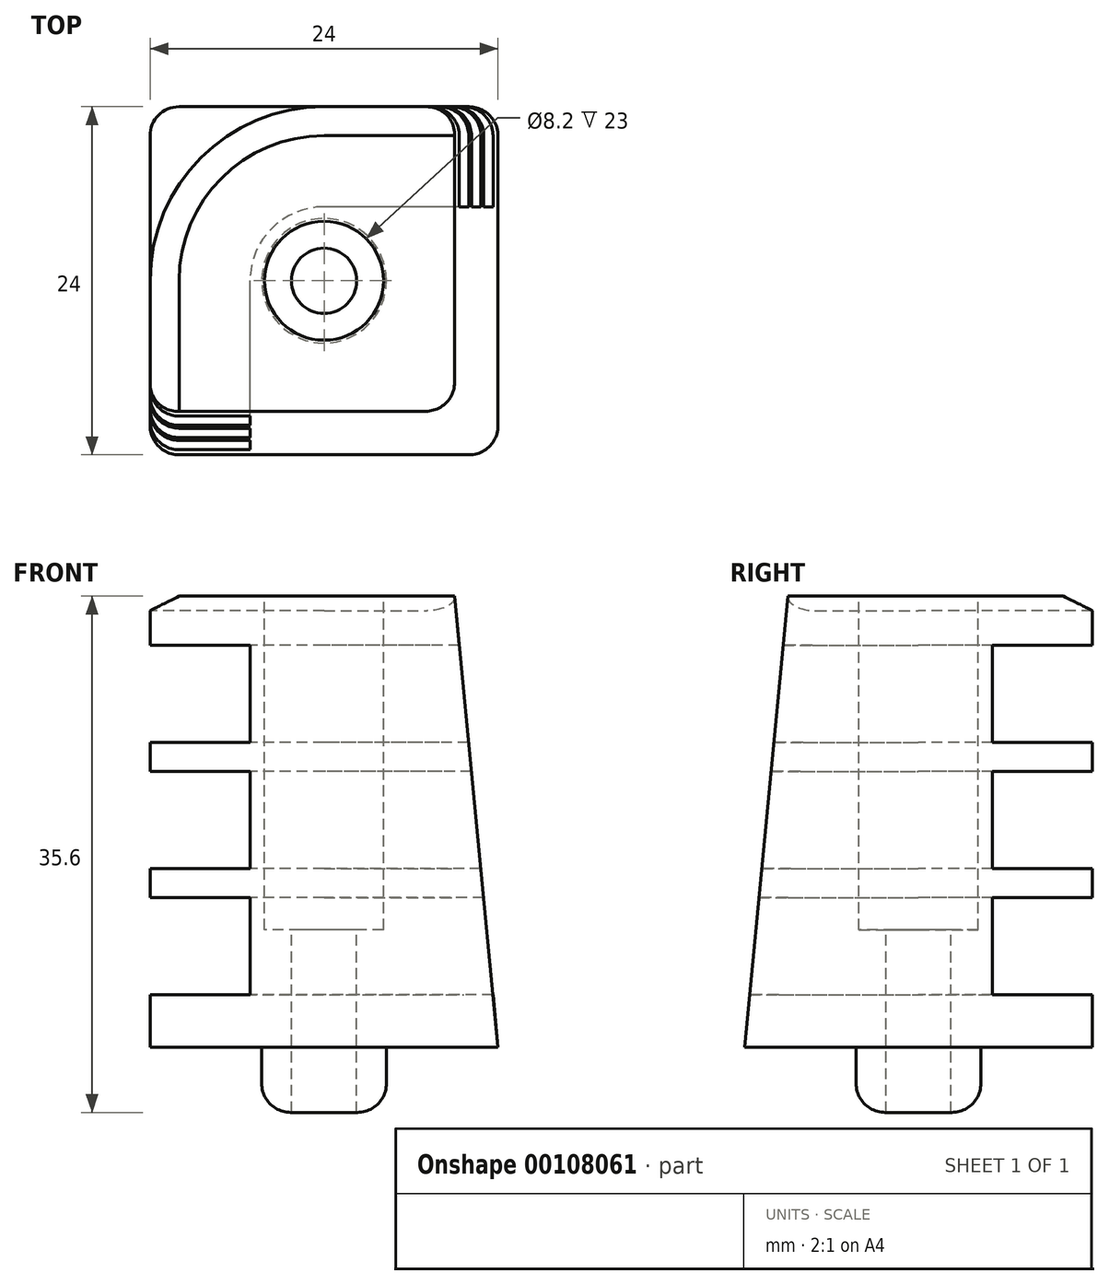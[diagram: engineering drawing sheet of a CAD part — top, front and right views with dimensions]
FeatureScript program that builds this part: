
annotation { "Feature Type Name" : "Feature", "Feature Type Description" : "" }
export const myFeature = defineFeature(function(context is Context, id is Id, definition is map)
    precondition{}
    {
        {
            var Q0;
            Q0=qCreatedBy(makeId("Top.planeOp"),FACE);
            var sketch = newSketch(context, id + "F0", { "sketchPlane" : qUnion([Q0])});
            skLineSegment(sketch, "E0.bottom", {"start": v(0, 0) * mm, "end": v(24, 0) * mm});
            skLineSegment(sketch, "E0.top", {"start": v(0, 24) * mm, "end": v(24, 24) * mm});
            skLineSegment(sketch, "E0.left", {"start": v(0, 0) * mm, "end": v(0, 24) * mm});
            skLineSegment(sketch, "E0.right", {"start": v(24, 0) * mm, "end": v(24, 24) * mm});
            skPoint(sketch, "E1.visualSharp", {"position": v(0, 24) * mm});
            skPoint(sketch, "E2.visualSharp", {"position": v(24, 24) * mm});
            skPoint(sketch, "E3.visualSharp", {"position": v(24, 0) * mm});
            skPoint(sketch, "E4.visualSharp", {"position": v(0, 0) * mm});
            skSolve(sketch);
        }
        {
            var Q0;
            Q0 = qSketchRegion(id + "F0", true);
            extrude(context, id + "F1", {"entities" : qUnion([Q0]), "depth" : 3.6 * mm});
        }
        {
            var Q0;
            Q0=makeQuery(id+"F1.opExtrude","CAP_FACE",FACE,{"disambiguationData":[OSD([sQuery(id+"F0.wireOp",EDGE,"E0.bottom"),sQuery(id+"F0.wireOp",EDGE,"E0.top"),sQuery(id+"F0.wireOp",EDGE,"E0.left"),sQuery(id+"F0.wireOp",EDGE,"E0.right"),sQuery(id+"F0.wireOp",EDGE,"E1.filletArc"),sQuery(id+"F0.wireOp",EDGE,"E2.filletArc"),sQuery(id+"F0.wireOp",EDGE,"E3.filletArc"),sQuery(id+"F0.wireOp",EDGE,"E4.filletArc")])],"isStart":true});
            var sketch = newSketch(context, id + "F2", { "sketchPlane" : qUnion([Q0])});
            skPoint(sketch, "E5.centerSnap0", {"position": v(12, -24) * mm});
            skPoint(sketch, "E6", {"position": v(24, -12) * mm});
            skCircle(sketch, "E7", {"center": v(12, -12) * mm, "radius": 4.3 * mm});
            skCircle(sketch, "E8", {"center": v(12, -12) * mm, "radius": 2.25 * mm});
            skSolve(sketch);
        }
        {
            var Q0;
            Q0=makeQuery(id+"F2.imprint","IMPRINT",FACE,{"disambiguationData":[TD([[makeQuery(id+"F2.imprint","IMPRINT",EDGE,{"derivedFrom":sQuery(id+"F2.wireOp",EDGE,"E7")}),1.0]])]});
            extrude(context, id + "F3", {"entities" : qUnion([Q0]), "operationType" : NewBodyOperationType.ADD, "depth" : 4.5 * mm});
        }
        {
            var Q0;
            Q0=makeQuery(id+"F3.boolean.opBoolean","SPLIT",FACE,{"disambiguationData":[TD([makeQuery(id+"F3.opExtrude","SWEPT_FACE",FACE,{"disambiguationData":[OSD([sQuery(id+"F2.wireOp",EDGE,"E8")])]})])],"derivedFrom":makeQuery(id+"F1.opExtrude","CAP_FACE",FACE,{"disambiguationData":[OSD([sQuery(id+"F0.wireOp",EDGE,"E0.bottom"),sQuery(id+"F0.wireOp",EDGE,"E0.top"),sQuery(id+"F0.wireOp",EDGE,"E0.left"),sQuery(id+"F0.wireOp",EDGE,"E0.right"),sQuery(id+"F0.wireOp",EDGE,"E1.filletArc"),sQuery(id+"F0.wireOp",EDGE,"E2.filletArc"),sQuery(id+"F0.wireOp",EDGE,"E3.filletArc")])],"isStart":true})});
            extrude(context, id + "F4", {"entities" : qUnion([Q0]), "operationType" : NewBodyOperationType.REMOVE, "oppositeDirection" : true, "depth" : 10 * mm});
        }
        {
            var Q0;
            Q0=makeQuery(id+"F1.opExtrude","CAP_FACE",FACE,{"disambiguationData":[OSD([sQuery(id+"F0.wireOp",EDGE,"E0.bottom"),sQuery(id+"F0.wireOp",EDGE,"E0.top"),sQuery(id+"F0.wireOp",EDGE,"E0.left"),sQuery(id+"F0.wireOp",EDGE,"E0.right"),sQuery(id+"F0.wireOp",EDGE,"E1.filletArc"),sQuery(id+"F0.wireOp",EDGE,"E2.filletArc"),sQuery(id+"F0.wireOp",EDGE,"E3.filletArc"),sQuery(id+"F0.wireOp",EDGE,"E4.filletArc")])],"isStart":false});
            var sketch = newSketch(context, id + "F5", { "sketchPlane" : qUnion([Q0])});
            skLineSegment(sketch, "E9.bottom", {"start": v(20, 0) * mm, "end": v(6.9, 0) * mm});
            skLineSegment(sketch, "E9.top", {"start": v(24, 17.1) * mm, "end": v(6.9, 17.1) * mm});
            skLineSegment(sketch, "E9.right", {"start": v(6.9, 0) * mm, "end": v(6.9, 17.1) * mm});
            skPoint(sketch, "E10.orphan", {"position": v(24, 0) * mm});
            skPoint(sketch, "E11.center.orphan", {"position": v(12, 12) * mm});
            skSolve(sketch);
        }
        {
            var Q0;
            {var subQ6=sQuery(id+"F5.wireOp",EDGE,"E9.bottom");Q0=makeQuery(id+"F5.imprint","IMPRINT",FACE,{"disambiguationData":[TD([[makeQuery(id+"F5.imprint","IMPRINT",EDGE,{"derivedFrom":subQ6}),1.0]])]});}
            extrude(context, id + "F6", {"entities" : qUnion([Q0]), "operationType" : NewBodyOperationType.ADD, "depth" : 6.7 * mm});
        }
        {
            var Q0;
            Q0=makeQuery(id+"F6.opExtrude","CAP_FACE",FACE,{"disambiguationData":[OSD([sQuery(id+"F0.wireOp",EDGE,"E0.bottom"),sQuery(id+"F0.wireOp",EDGE,"E0.top"),sQuery(id+"F0.wireOp",EDGE,"E0.left"),sQuery(id+"F0.wireOp",EDGE,"E0.right"),sQuery(id+"F2.wireOp",EDGE,"E8"),sQuery(id+"F5.wireOp",EDGE,"E9.bottom"),sQuery(id+"F5.wireOp",EDGE,"E9.top"),sQuery(id+"F5.wireOp",EDGE,"E9.right")])],"isStart":false});
            var sketch = newSketch(context, id + "F7", { "sketchPlane" : qUnion([Q0])});
            skLineSegment(sketch, "E12.bottom", {"start": v(0, 0) * mm, "end": v(24, 0) * mm});
            skLineSegment(sketch, "E12.top", {"start": v(0, 24) * mm, "end": v(24, 24) * mm});
            skLineSegment(sketch, "E12.left", {"start": v(0, 0) * mm, "end": v(0, 24) * mm});
            skLineSegment(sketch, "E12.right", {"start": v(24, 0) * mm, "end": v(24, 24) * mm});
            skSolve(sketch);
        }
        {
            var Q0;
            {var subQ2=sQuery(id+"F7.wireOp",EDGE,"E12.top");Q0=makeQuery(id+"F7.imprint","IMPRINT",FACE,{"disambiguationData":[TD([[makeQuery(id+"F7.imprint","IMPRINT",EDGE,{"derivedFrom":subQ2}),-1.0]])]});}
            var Q1;
            {var subQ1=makeQuery(id+"F6.opExtrude","CAP_EDGE",EDGE,{"disambiguationData":[OSD([sQuery(id+"F5.wireOp",EDGE,"E9.top")])],"isStart":false});Q1=makeQuery(id+"F7.imprint","IMPRINT",FACE,{"disambiguationData":[TD([[makeQuery(id+"F7.imprint","IMPRINT",EDGE,{"derivedFrom":subQ1}),1.0]])]});}
            extrude(context, id + "F8", {"entities" : qUnion([Q0, Q1]), "operationType" : NewBodyOperationType.ADD, "depth" : 2 * mm});
        }
        {
            var Q0;
            Q0=makeQuery(id+"F8.opExtrude","CAP_FACE",FACE,{"disambiguationData":[OSD([sQuery(id+"F0.wireOp",EDGE,"E0.bottom"),sQuery(id+"F0.wireOp",EDGE,"E0.top"),sQuery(id+"F0.wireOp",EDGE,"E0.left"),sQuery(id+"F0.wireOp",EDGE,"E0.right"),sQuery(id+"F2.wireOp",EDGE,"E8"),sQuery(id+"F7.wireOp",EDGE,"E12.bottom"),sQuery(id+"F7.wireOp",EDGE,"E12.top"),sQuery(id+"F7.wireOp",EDGE,"E12.left"),sQuery(id+"F7.wireOp",EDGE,"E12.right")])],"isStart":false});
            var sketch = newSketch(context, id + "F9", { "sketchPlane" : qUnion([Q0])});
            skLineSegment(sketch, "E13.bottom", {"start": v(24, 0) * mm, "end": v(6.9, 0) * mm});
            skLineSegment(sketch, "E13.top", {"start": v(24, 17.1) * mm, "end": v(6.9, 17.1) * mm});
            skLineSegment(sketch, "E13.left", {"start": v(24, 0) * mm, "end": v(24, 17.1) * mm});
            skLineSegment(sketch, "E13.right", {"start": v(6.9, 0) * mm, "end": v(6.9, 17.1) * mm});
            skSolve(sketch);
        }
        {
            var Q0;
            Q0=makeQuery(id+"F9.imprint","IMPRINT",FACE,{"disambiguationData":[TD([[makeQuery(id+"F9.imprint","IMPRINT",EDGE,{"derivedFrom":sQuery(id+"F9.wireOp",EDGE,"E13.bottom")}),1.0]])]});
            extrude(context, id + "F10", {"entities" : qUnion([Q0]), "operationType" : NewBodyOperationType.ADD, "depth" : 6.7 * mm});
        }
        {
            var Q0;
            Q0=makeQuery(id+"F10.opExtrude","CAP_FACE",FACE,{"disambiguationData":[OSD([sQuery(id+"F0.wireOp",EDGE,"E0.bottom"),sQuery(id+"F0.wireOp",EDGE,"E0.top"),sQuery(id+"F0.wireOp",EDGE,"E0.left"),sQuery(id+"F0.wireOp",EDGE,"E0.right"),sQuery(id+"F2.wireOp",EDGE,"E8"),sQuery(id+"F9.wireOp",EDGE,"E13.bottom"),sQuery(id+"F9.wireOp",EDGE,"E13.top"),sQuery(id+"F9.wireOp",EDGE,"E13.left"),sQuery(id+"F9.wireOp",EDGE,"E13.right")])],"isStart":false});
            var sketch = newSketch(context, id + "F11", { "sketchPlane" : qUnion([Q0])});
            skLineSegment(sketch, "E14.bottom", {"start": v(24, 0) * mm, "end": v(0, 0) * mm});
            skLineSegment(sketch, "E14.top", {"start": v(24, 24) * mm, "end": v(0, 24) * mm});
            skLineSegment(sketch, "E14.left", {"start": v(24, 0) * mm, "end": v(24, 24) * mm});
            skLineSegment(sketch, "E14.right", {"start": v(0, 0) * mm, "end": v(0, 24) * mm});
            skSolve(sketch);
        }
        {
            var Q0;
            {var subQ3=sQuery(id+"F11.wireOp",EDGE,"E14.top");Q0=makeQuery(id+"F11.imprint","IMPRINT",FACE,{"disambiguationData":[TD([[makeQuery(id+"F11.imprint","IMPRINT",EDGE,{"derivedFrom":subQ3}),1.0]])]});}
            var Q1;
            {var subQ1=makeQuery(id+"F10.opExtrude","CAP_EDGE",EDGE,{"disambiguationData":[OSD([sQuery(id+"F9.wireOp",EDGE,"E13.top")])],"isStart":false});Q1=makeQuery(id+"F11.imprint","IMPRINT",FACE,{"disambiguationData":[TD([[makeQuery(id+"F11.imprint","IMPRINT",EDGE,{"derivedFrom":subQ1}),1.0]])]});}
            extrude(context, id + "F12", {"entities" : qUnion([Q0, Q1]), "operationType" : NewBodyOperationType.ADD, "depth" : 2 * mm});
        }
        {
            var Q0;
            Q0=makeQuery(id+"F12.opExtrude","CAP_FACE",FACE,{"disambiguationData":[OSD([sQuery(id+"F0.wireOp",EDGE,"E0.bottom"),sQuery(id+"F0.wireOp",EDGE,"E0.top"),sQuery(id+"F0.wireOp",EDGE,"E0.left"),sQuery(id+"F0.wireOp",EDGE,"E0.right"),sQuery(id+"F2.wireOp",EDGE,"E8"),sQuery(id+"F11.wireOp",EDGE,"E14.bottom"),sQuery(id+"F11.wireOp",EDGE,"E14.top"),sQuery(id+"F11.wireOp",EDGE,"E14.left"),sQuery(id+"F11.wireOp",EDGE,"E14.right")])],"isStart":false});
            var sketch = newSketch(context, id + "F13", { "sketchPlane" : qUnion([Q0])});
            skLineSegment(sketch, "E15.bottom", {"start": v(24, 0) * mm, "end": v(6.9, 0) * mm});
            skLineSegment(sketch, "E15.top", {"start": v(24, 17.1) * mm, "end": v(6.9, 17.1) * mm});
            skLineSegment(sketch, "E15.left", {"start": v(24, 0) * mm, "end": v(24, 17.1) * mm});
            skLineSegment(sketch, "E15.right", {"start": v(6.9, 0) * mm, "end": v(6.9, 17.1) * mm});
            skSolve(sketch);
        }
        {
            var Q0;
            Q0 = qSketchRegion(id + "F13", true);
            extrude(context, id + "F14", {"entities" : qUnion([Q0]), "operationType" : NewBodyOperationType.ADD, "depth" : 6.7 * mm});
        }
        {
            var Q0;
            Q0=makeQuery(id+"F14.opExtrude","CAP_FACE",FACE,{"disambiguationData":[OSD([sQuery(id+"F13.wireOp",EDGE,"E15.bottom"),sQuery(id+"F13.wireOp",EDGE,"E15.top"),sQuery(id+"F13.wireOp",EDGE,"E15.left"),sQuery(id+"F13.wireOp",EDGE,"E15.right")])],"isStart":false});
            var sketch = newSketch(context, id + "F15", { "sketchPlane" : qUnion([Q0])});
            skLineSegment(sketch, "E16.bottom", {"start": v(24, 0) * mm, "end": v(0, 0) * mm});
            skLineSegment(sketch, "E16.top", {"start": v(24, 24) * mm, "end": v(0, 24) * mm});
            skLineSegment(sketch, "E16.left", {"start": v(24, 0) * mm, "end": v(24, 24) * mm});
            skLineSegment(sketch, "E16.right", {"start": v(0, 0) * mm, "end": v(0, 24) * mm});
            skSolve(sketch);
        }
        {
            var Q0;
            Q0 = qSketchRegion(id + "F15", true);
            extrude(context, id + "F16", {"entities" : qUnion([Q0]), "operationType" : NewBodyOperationType.ADD, "depth" : 3.4 * mm});
        }
        {
            var Q0;
            Q0=makeQuery(id+"F6.opExtrude","SWEPT_EDGE",EDGE,{"disambiguationData":[OSD([sQuery(id+"F5.wireOp",EDGE,"E9.top"),sQuery(id+"F5.wireOp",EDGE,"E9.right")])]});
            var Q1;
            Q1=makeQuery(id+"F10.opExtrude","SWEPT_EDGE",EDGE,{"disambiguationData":[OSD([sQuery(id+"F9.wireOp",EDGE,"E13.top"),sQuery(id+"F9.wireOp",EDGE,"E13.right")])]});
            var Q2;
            Q2=makeQuery(id+"F14.opExtrude","SWEPT_EDGE",EDGE,{"disambiguationData":[OSD([sQuery(id+"F13.wireOp",EDGE,"E15.top"),sQuery(id+"F13.wireOp",EDGE,"E15.right")])]});
            fillet(context, id + "F17", {"entities" : qUnion([Q0, Q1, Q2]), "radius" : 5.1 * mm, "tangentPropagation" : true, "allowEdgeOverflow" : false});
        }
        {
            var Q0;
            Q0=makeQuery(id+"F8.opExtrude","SWEPT_EDGE",EDGE,{"disambiguationData":[OSD([sQuery(id+"F7.wireOp",EDGE,"E12.top"),sQuery(id+"F7.wireOp",EDGE,"E12.left")])]});
            var Q1;
            Q1=makeQuery(id+"F12.opExtrude","SWEPT_EDGE",EDGE,{"disambiguationData":[OSD([sQuery(id+"F11.wireOp",EDGE,"E14.top"),sQuery(id+"F11.wireOp",EDGE,"E14.right")])]});
            var Q2;
            Q2=makeQuery(id+"F16.opExtrude","SWEPT_EDGE",EDGE,{"disambiguationData":[OSD([sQuery(id+"F15.wireOp",EDGE,"E16.top"),sQuery(id+"F15.wireOp",EDGE,"E16.right")])]});
            fillet(context, id + "F18", {"entities" : qUnion([Q0, Q1, Q2]), "radius" : 12 * mm, "tangentPropagation" : true, "allowEdgeOverflow" : false});
        }
        {
            var Q0;
            Q0=makeQuery(id+"F16.opExtrude","CAP_FACE",FACE,{"disambiguationData":[OSD([sQuery(id+"F15.wireOp",EDGE,"E16.bottom"),sQuery(id+"F15.wireOp",EDGE,"E16.top"),sQuery(id+"F15.wireOp",EDGE,"E16.left"),sQuery(id+"F15.wireOp",EDGE,"E16.right")])],"isStart":false});
            var sketch = newSketch(context, id + "F19", { "sketchPlane" : qUnion([Q0])});
            skCircle(sketch, "E17", {"center": v(12, 12) * mm, "radius": 4.1 * mm});
            skSolve(sketch);
        }
        {
            var Q0;
            Q0 = qSketchRegion(id + "F19", true);
            extrude(context, id + "F20", {"entities" : qUnion([Q0]), "operationType" : NewBodyOperationType.REMOVE, "oppositeDirection" : true, "depth" : 23 * mm});
        }
        {
            var Q0;
            {var subQ0=sQuery(id+"F0.wireOp",EDGE,"E0.right");Q0=makeQuery(id+"F16.boolean.opBoolean","MERGE",FACE,{"derivedFrom":[makeQuery(id+"F14.boolean.opBoolean","MERGE",FACE,{"derivedFrom":[makeQuery(id+"F12.boolean.opBoolean","MERGE",FACE,{"derivedFrom":[makeQuery(id+"F10.boolean.opBoolean","MERGE",FACE,{"derivedFrom":[makeQuery(id+"F8.boolean.opBoolean","MERGE",FACE,{"derivedFrom":[makeQuery(id+"F6.boolean.opBoolean","MERGE",FACE,{"derivedFrom":[makeQuery(id+"F1.opExtrude","SWEPT_FACE",FACE,{"disambiguationData":[OSD([subQ0])]}),makeQuery(id+"F6.opExtrude","SWEPT_FACE",FACE,{"disambiguationData":[OSD([subQ0])]})]}),makeQuery(id+"F8.opExtrude","SWEPT_FACE",FACE,{"disambiguationData":[OSD([sQuery(id+"F7.wireOp",EDGE,"E12.right")])]})]}),makeQuery(id+"F10.opExtrude","SWEPT_FACE",FACE,{"disambiguationData":[OSD([sQuery(id+"F9.wireOp",EDGE,"E13.left")])]})]}),makeQuery(id+"F12.opExtrude","SWEPT_FACE",FACE,{"disambiguationData":[OSD([sQuery(id+"F11.wireOp",EDGE,"E14.left")])]})]}),makeQuery(id+"F14.opExtrude","SWEPT_FACE",FACE,{"disambiguationData":[OSD([sQuery(id+"F13.wireOp",EDGE,"E15.left")])]})]}),makeQuery(id+"F16.opExtrude","SWEPT_FACE",FACE,{"disambiguationData":[OSD([sQuery(id+"F15.wireOp",EDGE,"E16.left")])]})]});}
            var sketch = newSketch(context, id + "F21", { "sketchPlane" : qUnion([Q0])});
            skLineSegment(sketch, "E18", {"start": v(0, 0) * mm, "end": v(3, 31.1) * mm});
            skSolve(sketch);
        }
        {
            var Q0;
            {var subQ0=sQuery(id+"F0.wireOp",EDGE,"E0.bottom");Q0=makeQuery(id+"F16.boolean.opBoolean","MERGE",FACE,{"derivedFrom":[makeQuery(id+"F14.boolean.opBoolean","MERGE",FACE,{"derivedFrom":[makeQuery(id+"F12.boolean.opBoolean","MERGE",FACE,{"derivedFrom":[makeQuery(id+"F10.boolean.opBoolean","MERGE",FACE,{"derivedFrom":[makeQuery(id+"F8.boolean.opBoolean","MERGE",FACE,{"derivedFrom":[makeQuery(id+"F6.boolean.opBoolean","MERGE",FACE,{"derivedFrom":[makeQuery(id+"F1.opExtrude","SWEPT_FACE",FACE,{"disambiguationData":[OSD([subQ0])]}),makeQuery(id+"F6.opExtrude","SWEPT_FACE",FACE,{"disambiguationData":[OSD([subQ0,sQuery(id+"F5.wireOp",EDGE,"E9.bottom")])]})]}),makeQuery(id+"F8.opExtrude","SWEPT_FACE",FACE,{"disambiguationData":[OSD([sQuery(id+"F7.wireOp",EDGE,"E12.bottom")])]})]}),makeQuery(id+"F10.opExtrude","SWEPT_FACE",FACE,{"disambiguationData":[OSD([sQuery(id+"F9.wireOp",EDGE,"E13.bottom")])]})]}),makeQuery(id+"F12.opExtrude","SWEPT_FACE",FACE,{"disambiguationData":[OSD([sQuery(id+"F11.wireOp",EDGE,"E14.bottom")])]})]}),makeQuery(id+"F14.opExtrude","SWEPT_FACE",FACE,{"disambiguationData":[OSD([sQuery(id+"F13.wireOp",EDGE,"E15.bottom")])]})]}),makeQuery(id+"F16.opExtrude","SWEPT_FACE",FACE,{"disambiguationData":[OSD([sQuery(id+"F15.wireOp",EDGE,"E16.bottom")])]})]});}
            var sketch = newSketch(context, id + "F22", { "sketchPlane" : qUnion([Q0])});
            skLineSegment(sketch, "E19", {"start": v(24, 0) * mm, "end": v(21, 31.1) * mm});
            skSolve(sketch);
        }
        {
            var Q0;
            {var subQ0=sQuery(id+"F21.wireOp",EDGE,"E18");Q0=makeQuery(id+"F21.imprint","IMPRINT",FACE,{"disambiguationData":[TD([[makeQuery(id+"F21.imprint","IMPRINT",EDGE,{"derivedFrom":subQ0}),1.0]])]});}
            extrude(context, id + "F23", {"entities" : qUnion([Q0]), "operationType" : NewBodyOperationType.ADD, "depth" : 25 * mm});
        }
        {
            var Q0;
            {var subQ0=sQuery(id+"F22.wireOp",EDGE,"E19");Q0=makeQuery(id+"F22.imprint","IMPRINT",FACE,{"disambiguationData":[TD([[makeQuery(id+"F22.imprint","IMPRINT",EDGE,{"derivedFrom":subQ0}),-1.0]])]});}
            extrude(context, id + "F24", {"entities" : qUnion([Q0]), "operationType" : NewBodyOperationType.REMOVE, "oppositeDirection" : true, "depth" : 25 * mm});
        }
        {
            var Q0;
            Q0=makeQuery(id+"F23.opExtrude","CAP_FACE",FACE,{"disambiguationData":[OSD([sQuery(id+"F0.wireOp",EDGE,"E0.bottom"),sQuery(id+"F0.wireOp",EDGE,"E0.right"),sQuery(id+"F7.wireOp",EDGE,"E12.bottom"),sQuery(id+"F7.wireOp",EDGE,"E12.right"),sQuery(id+"F9.wireOp",EDGE,"E13.bottom"),sQuery(id+"F9.wireOp",EDGE,"E13.left"),sQuery(id+"F11.wireOp",EDGE,"E14.bottom"),sQuery(id+"F11.wireOp",EDGE,"E14.left"),sQuery(id+"F13.wireOp",EDGE,"E15.bottom"),sQuery(id+"F13.wireOp",EDGE,"E15.left"),sQuery(id+"F15.wireOp",EDGE,"E16.bottom"),sQuery(id+"F15.wireOp",EDGE,"E16.left"),sQuery(id+"F21.wireOp",EDGE,"E18")])],"isStart":false});
            extrude(context, id + "F25", {"entities" : qUnion([Q0]), "operationType" : NewBodyOperationType.REMOVE, "oppositeDirection" : true, "depth" : 50 * mm});
        }
        {
            var Q0;
            Q0=makeQuery(id+"F16.opExtrude","CAP_EDGE",EDGE,{"disambiguationData":[OSD([sQuery(id+"F15.wireOp",EDGE,"E16.right")])],"isStart":false});
            var Q1;
            Q1=makeQuery(id+"F25.boolean.opBoolean","COPY",EDGE,{"derivedFrom":makeQuery(id+"F25.opExtrude","SWEPT_EDGE",EDGE,{"disambiguationData":[OSD([sQuery(id+"F15.wireOp",EDGE,"E16.left"),sQuery(id+"F21.wireOp",EDGE,"E18")])]})});
            var Q2;
            Q2=makeQuery(id+"F24.boolean.opBoolean","COPY",EDGE,{"derivedFrom":makeQuery(id+"F24.opExtrude","SWEPT_EDGE",EDGE,{"disambiguationData":[OSD([sQuery(id+"F15.wireOp",EDGE,"E16.bottom"),sQuery(id+"F22.wireOp",EDGE,"E19")])]})});
            chamfer(context, id + "F26", {"entities" : qUnion([Q0, Q1, Q2]), "chamferType" : ChamferType.TWO_OFFSETS, "width1" : 1 * mm, "oppositeDirection" : false, "width2" : 2 * mm, "tangentPropagation" : true});
        }
        {
            var Q0;
            Q0=makeQuery(id+"F25.boolean.opBoolean","INTERSECT",EDGE,{"derivedFrom":[makeQuery(id+"F24.boolean.opBoolean","COPY",FACE,{"derivedFrom":makeQuery(id+"F24.opExtrude","SWEPT_FACE",FACE,{"disambiguationData":[OSD([sQuery(id+"F22.wireOp",EDGE,"E19")])]})}),makeQuery(id+"F25.opExtrude","SWEPT_FACE",FACE,{"disambiguationData":[OSD([sQuery(id+"F21.wireOp",EDGE,"E18")])]})]});
            fillet(context, id + "F27", {"entities" : qUnion([Q0]), "radius" : 2 * mm, "tangentPropagation" : true, "allowEdgeOverflow" : false});
        }
        {
            var Q0;
            Q0=makeQuery(id+"F25.boolean.opBoolean","INTERSECT",EDGE,{"derivedFrom":[makeQuery(id+"F16.opExtrude","SWEPT_FACE",FACE,{"disambiguationData":[OSD([sQuery(id+"F15.wireOp",EDGE,"E16.right")])]}),makeQuery(id+"F25.opExtrude","SWEPT_FACE",FACE,{"disambiguationData":[OSD([sQuery(id+"F21.wireOp",EDGE,"E18")])]})]});
            var Q1;
            Q1=makeQuery(id+"F25.boolean.opBoolean","INTERSECT",EDGE,{"derivedFrom":[makeQuery(id+"F12.opExtrude","SWEPT_FACE",FACE,{"disambiguationData":[OSD([sQuery(id+"F11.wireOp",EDGE,"E14.right")])]}),makeQuery(id+"F25.opExtrude","SWEPT_FACE",FACE,{"disambiguationData":[OSD([sQuery(id+"F21.wireOp",EDGE,"E18")])]})]});
            var Q2;
            Q2=makeQuery(id+"F25.boolean.opBoolean","INTERSECT",EDGE,{"derivedFrom":[makeQuery(id+"F8.opExtrude","SWEPT_FACE",FACE,{"disambiguationData":[OSD([sQuery(id+"F7.wireOp",EDGE,"E12.left")])]}),makeQuery(id+"F25.opExtrude","SWEPT_FACE",FACE,{"disambiguationData":[OSD([sQuery(id+"F21.wireOp",EDGE,"E18")])]})]});
            var Q3;
            Q3=makeQuery(id+"F25.boolean.opBoolean","INTERSECT",EDGE,{"derivedFrom":[makeQuery(id+"F1.opExtrude","SWEPT_FACE",FACE,{"disambiguationData":[OSD([sQuery(id+"F0.wireOp",EDGE,"E0.left")])]}),makeQuery(id+"F25.opExtrude","SWEPT_FACE",FACE,{"disambiguationData":[OSD([sQuery(id+"F21.wireOp",EDGE,"E18")])]})]});
            var Q4;
            Q4=makeQuery(id+"F1.opExtrude","SWEPT_EDGE",EDGE,{"disambiguationData":[OSD([sQuery(id+"F0.wireOp",EDGE,"E0.top"),sQuery(id+"F0.wireOp",EDGE,"E0.left")])]});
            var Q5;
            Q5=makeQuery(id+"F24.boolean.opBoolean","INTERSECT",EDGE,{"derivedFrom":[makeQuery(id+"F1.opExtrude","SWEPT_FACE",FACE,{"disambiguationData":[OSD([sQuery(id+"F0.wireOp",EDGE,"E0.top")])]}),makeQuery(id+"F24.opExtrude","SWEPT_FACE",FACE,{"disambiguationData":[OSD([sQuery(id+"F22.wireOp",EDGE,"E19")])]})]});
            var Q6;
            Q6=makeQuery(id+"F24.boolean.opBoolean","INTERSECT",EDGE,{"derivedFrom":[makeQuery(id+"F8.opExtrude","SWEPT_FACE",FACE,{"disambiguationData":[OSD([sQuery(id+"F7.wireOp",EDGE,"E12.top")])]}),makeQuery(id+"F24.opExtrude","SWEPT_FACE",FACE,{"disambiguationData":[OSD([sQuery(id+"F22.wireOp",EDGE,"E19")])]})]});
            var Q7;
            Q7=makeQuery(id+"F24.boolean.opBoolean","INTERSECT",EDGE,{"derivedFrom":[makeQuery(id+"F12.opExtrude","SWEPT_FACE",FACE,{"disambiguationData":[OSD([sQuery(id+"F11.wireOp",EDGE,"E14.top")])]}),makeQuery(id+"F24.opExtrude","SWEPT_FACE",FACE,{"disambiguationData":[OSD([sQuery(id+"F22.wireOp",EDGE,"E19")])]})]});
            var Q8;
            Q8=makeQuery(id+"F24.boolean.opBoolean","INTERSECT",EDGE,{"derivedFrom":[makeQuery(id+"F16.opExtrude","SWEPT_FACE",FACE,{"disambiguationData":[OSD([sQuery(id+"F15.wireOp",EDGE,"E16.top")])]}),makeQuery(id+"F24.opExtrude","SWEPT_FACE",FACE,{"disambiguationData":[OSD([sQuery(id+"F22.wireOp",EDGE,"E19")])]})]});
            fillet(context, id + "F28", {"entities" : qUnion([Q0, Q1, Q2, Q3, Q4, Q5, Q6, Q7, Q8]), "radius" : 2 * mm, "tangentPropagation" : true, "allowEdgeOverflow" : false});
        }
        {
            var Q0;
            Q0=makeQuery(id+"F3.opExtrude","CAP_EDGE",EDGE,{"disambiguationData":[OSD([sQuery(id+"F2.wireOp",EDGE,"E7")])],"isStart":false});
            fillet(context, id + "F29", {"entities" : qUnion([Q0]), "radius" : 2 * mm, "tangentPropagation" : true, "allowEdgeOverflow" : false});
        }
    });
